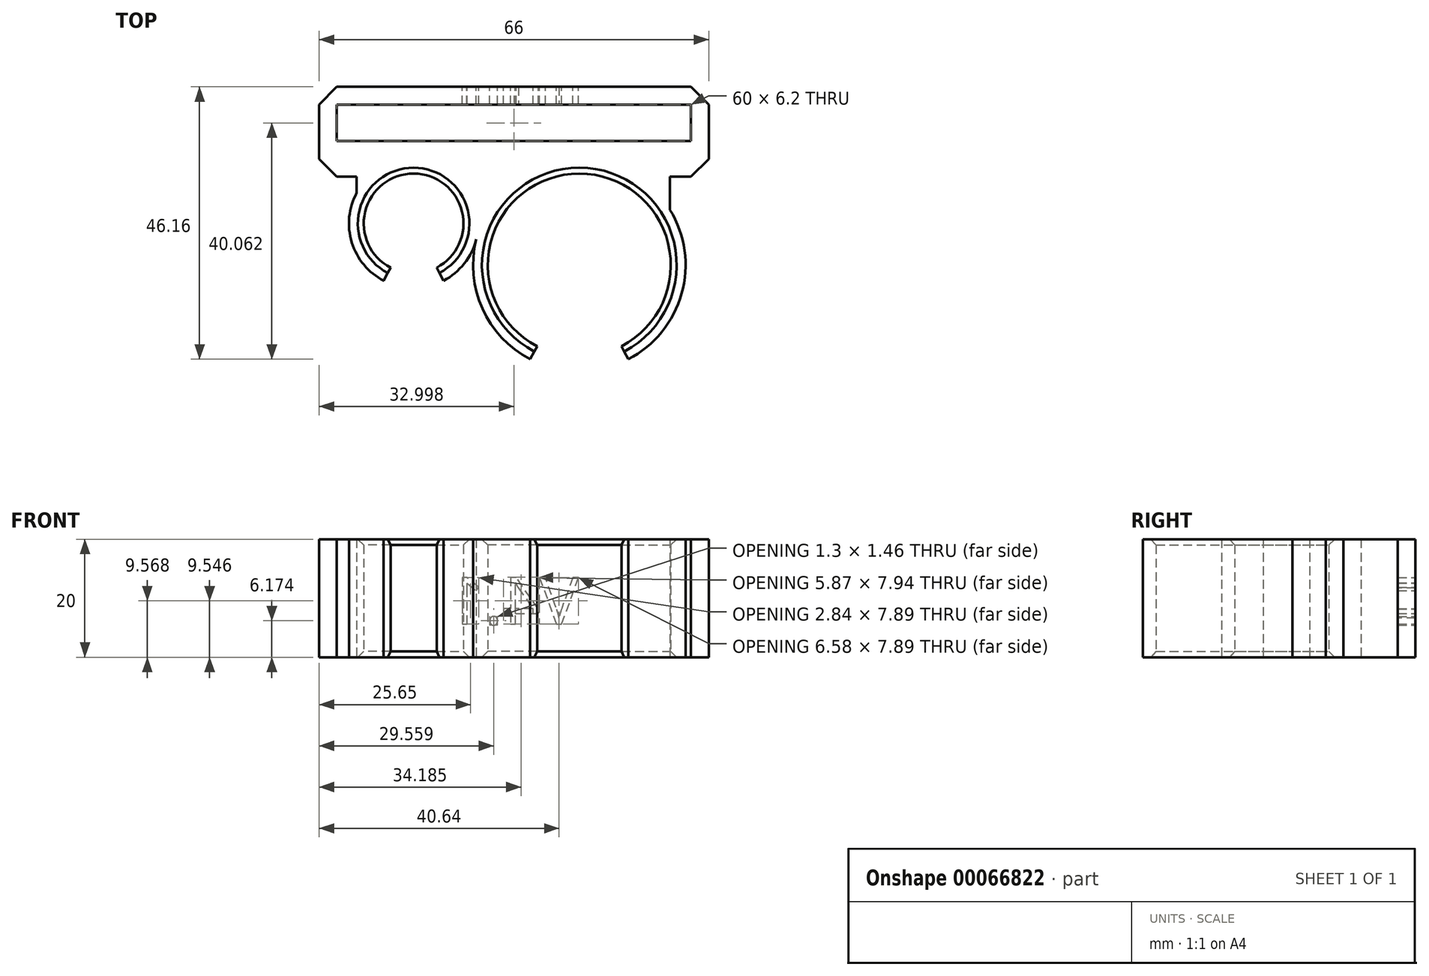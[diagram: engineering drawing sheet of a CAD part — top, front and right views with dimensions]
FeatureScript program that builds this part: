
annotation { "Feature Type Name" : "Feature", "Feature Type Description" : "" }
export const myFeature = defineFeature(function(context is Context, id is Id, definition is map)
    precondition{}
    {
        {
            var Q0;
            Q0=qCreatedBy(makeId("Top.planeOp"),FACE);
            var sketch = newSketch(context, id + "F0", { "sketchPlane" : qUnion([Q0])});
            skLineSegment(sketch, "E0.bottom", {"start": v(0.8, -2.56) * mm, "end": v(60.8, -2.56) * mm});
            skLineSegment(sketch, "E0.top", {"start": v(0.8, -8.76) * mm, "end": v(60.8, -8.76) * mm});
            skLineSegment(sketch, "E0.left", {"start": v(0.8, -2.56) * mm, "end": v(0.8, -8.76) * mm});
            skLineSegment(sketch, "E0.right", {"start": v(60.8, -2.56) * mm, "end": v(60.8, -8.76) * mm});
            skLineSegment(sketch, "E1.0", {"start": v(-2.2, -11.76) * mm, "end": v(63.8, -11.76) * mm});
            skLineSegment(sketch, "E1.1", {"start": v(-2.2, 0.44) * mm, "end": v(-2.2, -11.76) * mm});
            skLineSegment(sketch, "E1.2", {"start": v(-2.2, 0.44) * mm, "end": v(63.8, 0.44) * mm});
            skLineSegment(sketch, "E1.3", {"start": v(63.8, 0.44) * mm, "end": v(63.8, -11.76) * mm});
            skLineSegment(sketch, "E2", {"start": v(13.8, -11.76) * mm, "end": v(13.8, -33.66) * mm, "construction": true});
            skLineSegment(sketch, "E3", {"start": v(41.89, -11.76) * mm, "end": v(41.89, -47.76) * mm, "construction": true});
            skCircle(sketch, "E4", {"center": v(13.8, -22.7) * mm, "radius": 10.95 * mm});
            skCircle(sketch, "E5", {"center": v(41.89, -29.76) * mm, "radius": 18 * mm});
            skCircle(sketch, "E6.0", {"center": v(13.8, -22.7) * mm, "radius": 8.45 * mm});
            skCircle(sketch, "E7.0", {"center": v(41.89, -29.76) * mm, "radius": 15.5 * mm});
            skLineSegment(sketch, "E8", {"start": v(-2.2, -11.76) * mm, "end": v(-2.2, -14.76) * mm});
            skLineSegment(sketch, "E9", {"start": v(-2.2, -14.76) * mm, "end": v(6.28, -14.76) * mm});
            skLineSegment(sketch, "E10", {"start": v(63.8, -11.76) * mm, "end": v(63.8, -14.76) * mm});
            skLineSegment(sketch, "E11", {"start": v(63.8, -14.76) * mm, "end": v(51.84, -14.76) * mm});
            skLineSegment(sketch, "E12", {"start": v(57.26, -20.4) * mm, "end": v(57.26, -14.76) * mm});
            skLineSegment(sketch, "E13", {"start": v(4.18, -17.5) * mm, "end": v(4.18, -14.76) * mm});
            skPoint(sketch, "E13.endSnap0", {"position": v(2.04, -14.76) * mm});
            skSolve(sketch);
        }
        {
            var Q0;
            Q0=makeQuery(id+"F0.imprint","IMPRINT",FACE,{"disambiguationData":[TD([[makeQuery(id+"F0.imprint","IMPRINT",EDGE,{"derivedFrom":sQuery(id+"F0.wireOp",EDGE,"E0.bottom")}),1.0]])]});
            var Q1;
            Q1=makeQuery(id+"F0.imprint","IMPRINT",FACE,{"disambiguationData":[TD([[makeQuery(id+"F0.imprint","IMPRINT",EDGE,{"derivedFrom":sQuery(id+"F0.wireOp",EDGE,"E4")}),1.0]])]});
            var Q2;
            Q2=makeQuery(id+"F0.imprint","IMPRINT",FACE,{"disambiguationData":[TD([[makeQuery(id+"F0.imprint","IMPRINT",EDGE,{"derivedFrom":sQuery(id+"F0.wireOp",EDGE,"E5")}),1.0]])]});
            var Q3;
            {var subQ0=sQuery(id+"F0.wireOp",EDGE,"E10");Q3=makeQuery(id+"F0.imprint","IMPRINT",FACE,{"disambiguationData":[TD([[makeQuery(id+"F0.imprint","IMPRINT",EDGE,{"derivedFrom":subQ0}),-1.0]])]});}
            var Q4;
            {var subQ0=sQuery(id+"F0.wireOp",EDGE,"E8");Q4=makeQuery(id+"F0.imprint","IMPRINT",FACE,{"disambiguationData":[TD([[makeQuery(id+"F0.imprint","IMPRINT",EDGE,{"derivedFrom":subQ0}),1.0]])]});}
            var Q5;
            {var subQ0=sQuery(id+"F0.wireOp",EDGE,"E4");var subQ1=sQuery(id+"F0.wireOp",EDGE,"E1.0");var subQ2=makeQuery(id+"F0.imprint","INTERSECT",VERTEX,{"derivedFrom":[subQ1,subQ0]});Q5=makeQuery(id+"F0.imprint","IMPRINT",FACE,{"disambiguationData":[TD([[makeQuery(id+"F0.imprint","IMPRINT",EDGE,{"disambiguationData":[TD([[subQ2,-1.0]])],"derivedFrom":subQ1}),-1.0]])]});}
            var Q6;
            {var subQ3=sQuery(id+"F0.wireOp",EDGE,"E12");Q6=makeQuery(id+"F0.imprint","IMPRINT",FACE,{"disambiguationData":[TD([[makeQuery(id+"F0.imprint","IMPRINT",EDGE,{"derivedFrom":subQ3}),1.0]])]});}
            var Q7;
            {var subQ3=sQuery(id+"F0.wireOp",EDGE,"E13");Q7=makeQuery(id+"F0.imprint","IMPRINT",FACE,{"disambiguationData":[TD([[makeQuery(id+"F0.imprint","IMPRINT",EDGE,{"derivedFrom":subQ3}),-1.0]])]});}
            extrude(context, id + "F1", {"entities" : qUnion([Q0, Q1, Q2, Q3, Q4, Q5, Q6, Q7]), "depth" : 20 * mm});
        }
        {
            var Q0;
            Q0=makeQuery(id+"F1.opExtrude","CAP_EDGE",EDGE,{"disambiguationData":[OSD([sQuery(id+"F0.wireOp",EDGE,"E7.0")])],"isStart":false});
            var Q1;
            Q1=makeQuery(id+"F1.opExtrude","CAP_EDGE",EDGE,{"disambiguationData":[OSD([sQuery(id+"F0.wireOp",EDGE,"E6.0")])],"isStart":false});
            chamfer(context, id + "F2", {"entities" : qUnion([Q0, Q1]), "width" : 1 * mm, "tangentPropagation" : true});
        }
        {
            var Q0;
            Q0=sQuery(id+"F0.wireOp",VERTEX,"E5.center");
            var Q1;
            Q1=qCreatedBy(makeId("Right.planeOp"),FACE);
            cPlane(context, id + "F3", {"entities" : qUnion([Q0, Q1]), "cplaneType" : CPlaneType.PLANE_POINT, "offset" : 150 * mm, "width" : 150 * mm, "height" : 150 * mm});
        }
        {
            var Q0;
            Q0=qCreatedBy(id+"F3.planeOp",FACE);
            var sketch = newSketch(context, id + "F4", { "sketchPlane" : qUnion([Q0])});
            skPoint(sketch, "E14.0", {"position": v(-29.76, 0) * mm});
            skLineSegment(sketch, "E15.bottom", {"start": v(-29.76, 0) * mm, "end": v(-77.92, 0) * mm});
            skLineSegment(sketch, "E15.top", {"start": v(-29.76, 40.45) * mm, "end": v(-77.92, 40.45) * mm});
            skLineSegment(sketch, "E15.left", {"start": v(-29.76, 0) * mm, "end": v(-29.76, 40.45) * mm});
            skLineSegment(sketch, "E15.right", {"start": v(-77.92, 0) * mm, "end": v(-77.92, 40.45) * mm});
            skSolve(sketch);
        }
        {
            var Q0;
            Q0=makeQuery(id+"F4.imprint","IMPRINT",FACE,{"disambiguationData":[TD([[makeQuery(id+"F4.imprint","IMPRINT",EDGE,{"derivedFrom":sQuery(id+"F4.wireOp",EDGE,"E15.bottom")}),-1.0]])]});
            var Q1;
            Q1=sQuery(id+"F4.wireOp",EDGE,"E15.left");
            revolve(context, id + "F5", {"operationType" : NewBodyOperationType.REMOVE, "entities" : qUnion([Q0]), "axis" : qUnion([Q1]), "revolveType" : RevolveType.SYMMETRIC, "oppositeDirection" : true, "angle" : 55 * degree});
        }
        {
            var Q0;
            Q0=sQuery(id+"F0.wireOp",VERTEX,"E4.center");
            var Q1;
            Q1=qCreatedBy(makeId("Right.planeOp"),FACE);
            cPlane(context, id + "F6", {"entities" : qUnion([Q0, Q1]), "cplaneType" : CPlaneType.PLANE_POINT, "offset" : 150 * mm, "width" : 150 * mm, "height" : 150 * mm});
        }
        {
            var Q0;
            Q0=qCreatedBy(id+"F6.planeOp",FACE);
            var sketch = newSketch(context, id + "F7", { "sketchPlane" : qUnion([Q0])});
            skPoint(sketch, "E16.0", {"position": v(-22.7, 0) * mm});
            skLineSegment(sketch, "E17.bottom", {"start": v(-22.7, 0) * mm, "end": v(-92.36, 0) * mm});
            skLineSegment(sketch, "E17.top", {"start": v(-22.7, 48.2) * mm, "end": v(-92.36, 48.2) * mm});
            skLineSegment(sketch, "E17.left", {"start": v(-22.7, 0) * mm, "end": v(-22.7, 48.2) * mm});
            skLineSegment(sketch, "E17.right", {"start": v(-92.36, 0) * mm, "end": v(-92.36, 48.2) * mm});
            skSolve(sketch);
        }
        {
            var Q0;
            Q0=makeQuery(id+"F7.imprint","IMPRINT",FACE,{"disambiguationData":[TD([[makeQuery(id+"F7.imprint","IMPRINT",EDGE,{"derivedFrom":sQuery(id+"F7.wireOp",EDGE,"E17.bottom")}),-1.0]])]});
            var Q1;
            Q1=sQuery(id+"F7.wireOp",EDGE,"E17.left");
            revolve(context, id + "F8", {"operationType" : NewBodyOperationType.REMOVE, "entities" : qUnion([Q0]), "axis" : qUnion([Q1]), "revolveType" : RevolveType.SYMMETRIC, "oppositeDirection" : true, "angle" : 55 * degree});
        }
        {
            var Q0;
            Q0=makeQuery(id+"F1.opExtrude","SWEPT_EDGE",EDGE,{"disambiguationData":[OSD([sQuery(id+"F0.wireOp",EDGE,"E10"),sQuery(id+"F0.wireOp",EDGE,"E11")])]});
            chamfer(context, id + "F9", {"entities" : qUnion([Q0]), "width" : 3 * mm, "tangentPropagation" : true});
        }
        {
            var Q0;
            Q0=makeQuery(id+"F1.opExtrude","SWEPT_EDGE",EDGE,{"disambiguationData":[OSD([sQuery(id+"F0.wireOp",EDGE,"E8"),sQuery(id+"F0.wireOp",EDGE,"E9")])]});
            chamfer(context, id + "F10", {"entities" : qUnion([Q0]), "width" : 3 * mm, "tangentPropagation" : true});
        }
        {
            var Q0;
            Q0=makeQuery(id+"F1.opExtrude","SWEPT_EDGE",EDGE,{"disambiguationData":[OSD([sQuery(id+"F0.wireOp",EDGE,"E1.1"),sQuery(id+"F0.wireOp",EDGE,"E1.2")])]});
            var Q1;
            Q1=makeQuery(id+"F1.opExtrude","SWEPT_EDGE",EDGE,{"disambiguationData":[OSD([sQuery(id+"F0.wireOp",EDGE,"E1.2"),sQuery(id+"F0.wireOp",EDGE,"E1.3")])]});
            chamfer(context, id + "F11", {"entities" : qUnion([Q0, Q1]), "width" : 3 * mm, "tangentPropagation" : true});
        }
        {
            var Q0;
            Q0=makeQuery(id+"F1.opExtrude","CAP_EDGE",EDGE,{"disambiguationData":[OSD([sQuery(id+"F0.wireOp",EDGE,"E7.0")])],"isStart":true});
            var Q1;
            Q1=makeQuery(id+"F1.opExtrude","CAP_EDGE",EDGE,{"disambiguationData":[OSD([sQuery(id+"F0.wireOp",EDGE,"E6.0")])],"isStart":true});
            chamfer(context, id + "F12", {"entities" : qUnion([Q0, Q1]), "width" : 1 * mm, "tangentPropagation" : true});
        }
        {
            var Q0;
            Q0=makeQuery(id+"F1.opExtrude","SWEPT_FACE",FACE,{"disambiguationData":[OSD([sQuery(id+"F0.wireOp",EDGE,"E1.2")])]});
            var sketch = newSketch(context, id + "F13", { "sketchPlane" : qUnion([Q0])});
            skText(sketch, "E18", { "text": "V4.1", "fontName": "OpenSans-Regular.ttf"});
            const initialGuessF13  = {"E18": [-0.04174, 0.0056, 1, 0, 0.00796]};
            skSetInitialGuess(sketch, initialGuessF13);
            skSolve(sketch);
        }
        {
            var Q0;
            Q0 = qSketchRegion(id + "F13", true);
            extrude(context, id + "F14", {"entities" : qUnion([Q0]), "operationType" : NewBodyOperationType.REMOVE, "oppositeDirection" : true, "depth" : 4 * mm});
        }
        {
            var Q0;
            Q0=makeQuery(id+"F14.boolean.opBoolean","COPY",FACE,{"derivedFrom":makeQuery(id+"F14.opExtrude","SWEPT_FACE",FACE,{"disambiguationData":[OSD([sQuery(id+"F13.wireOp",EDGE,"E18.sketch_text.stroke-25")])]})});
            extrude(context, id + "F15", {"entities" : qUnion([Q0]), "endBound" : BoundingType.UP_TO_NEXT, "depth" : 25 * mm});
        }
    });
